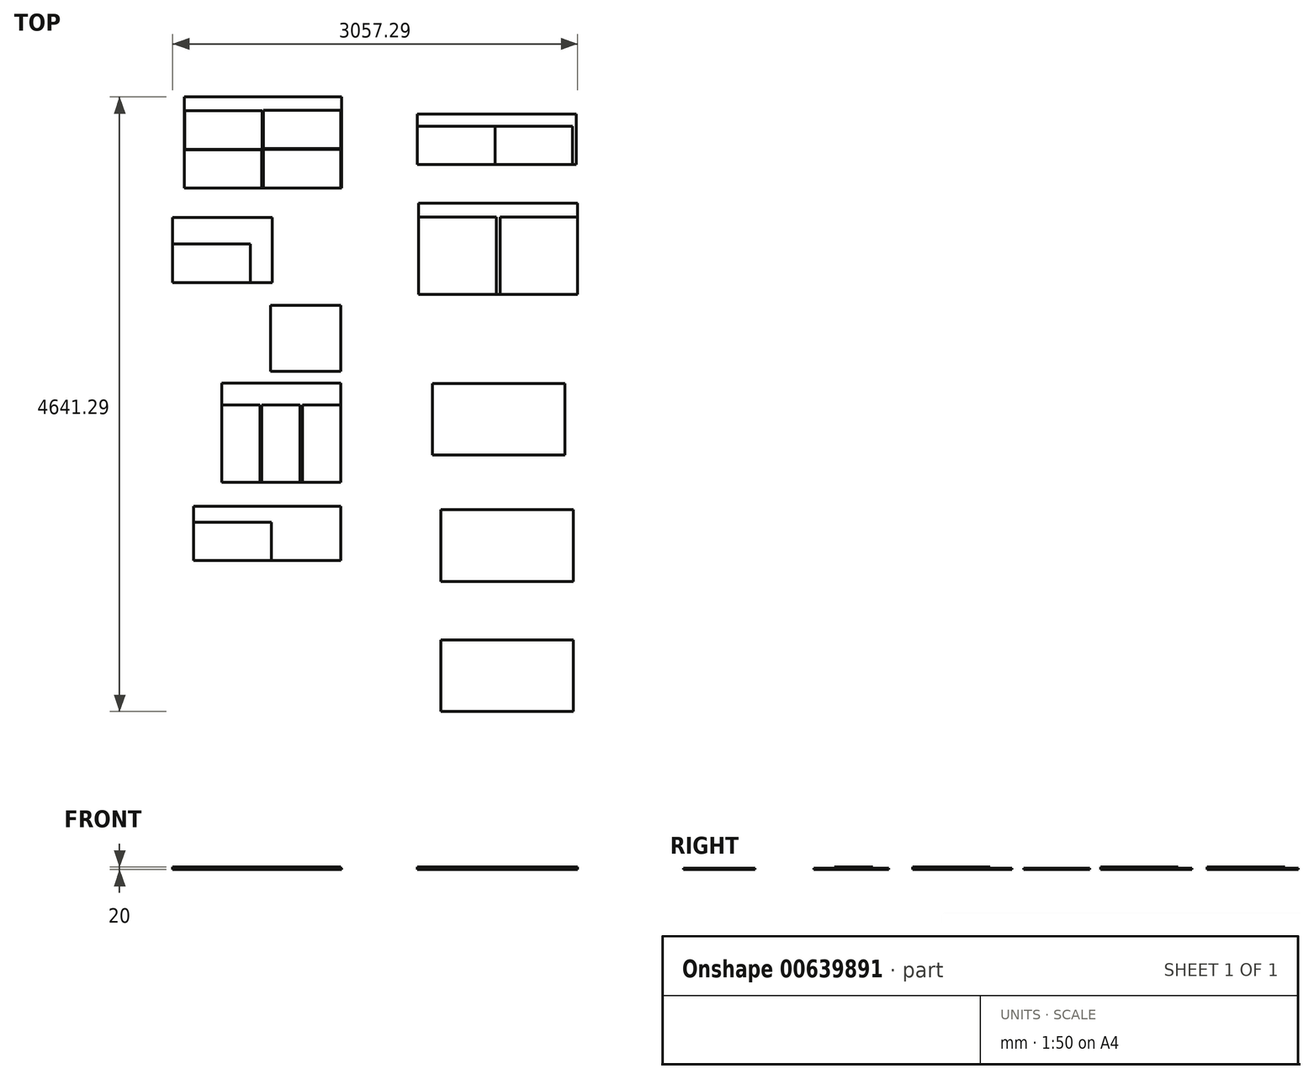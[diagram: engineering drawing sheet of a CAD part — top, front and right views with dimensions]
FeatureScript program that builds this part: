
annotation { "Feature Type Name" : "Feature", "Feature Type Description" : "" }
export const myFeature = defineFeature(function(context is Context, id is Id, definition is map)
    precondition{}
    {
        {
            var Q0;
            Q0=qCreatedBy(makeId("Top.planeOp"),FACE);
            var sketch = newSketch(context, id + "F0", { "sketchPlane" : qUnion([Q0])});
            skLineSegment(sketch, "E0.bottom", {"start": v(-1231.93, 732.64) * mm, "end": v(-41.93, 732.64) * mm});
            skLineSegment(sketch, "E0.top", {"start": v(-1231.93, 42.64) * mm, "end": v(-41.93, 42.64) * mm});
            skLineSegment(sketch, "E0.left", {"start": v(-1231.93, 732.64) * mm, "end": v(-1231.93, 42.64) * mm});
            skLineSegment(sketch, "E0.right", {"start": v(-41.93, 732.64) * mm, "end": v(-41.93, 42.64) * mm});
            skLineSegment(sketch, "E1.bottom", {"start": v(-1318.25, -179.37) * mm, "end": v(-568.25, -179.37) * mm});
            skLineSegment(sketch, "E1.top", {"start": v(-1318.25, -669.37) * mm, "end": v(-568.25, -669.37) * mm});
            skLineSegment(sketch, "E1.left", {"start": v(-1318.25, -179.37) * mm, "end": v(-1318.25, -669.37) * mm});
            skLineSegment(sketch, "E1.right", {"start": v(-568.25, -179.37) * mm, "end": v(-568.25, -669.37) * mm});
            skLineSegment(sketch, "E2.bottom", {"start": v(-579.3, -841.18) * mm, "end": v(-49.3, -841.18) * mm});
            skLineSegment(sketch, "E2.top", {"start": v(-579.3, -1341.18) * mm, "end": v(-49.3, -1341.18) * mm});
            skLineSegment(sketch, "E2.left", {"start": v(-579.3, -841.18) * mm, "end": v(-579.3, -1341.18) * mm});
            skLineSegment(sketch, "E2.right", {"start": v(-49.3, -841.18) * mm, "end": v(-49.3, -1341.18) * mm});
            skLineSegment(sketch, "E3.bottom", {"start": v(-949.3, -1429.12) * mm, "end": v(-49.3, -1429.12) * mm});
            skLineSegment(sketch, "E3.top", {"start": v(-949.3, -2179.12) * mm, "end": v(-49.3, -2179.12) * mm});
            skLineSegment(sketch, "E3.left", {"start": v(-949.3, -1429.12) * mm, "end": v(-949.3, -2179.12) * mm});
            skLineSegment(sketch, "E3.right", {"start": v(-49.3, -1429.12) * mm, "end": v(-49.3, -2179.12) * mm});
            skLineSegment(sketch, "E4.bottom", {"start": v(-1159.3, -2359.48) * mm, "end": v(-49.3, -2359.48) * mm});
            skLineSegment(sketch, "E4.top", {"start": v(-1159.3, -2769.48) * mm, "end": v(-49.3, -2769.48) * mm});
            skLineSegment(sketch, "E4.left", {"start": v(-1159.3, -2359.48) * mm, "end": v(-1159.3, -2769.48) * mm});
            skLineSegment(sketch, "E4.right", {"start": v(-49.3, -2359.48) * mm, "end": v(-49.3, -2769.48) * mm});
            skLineSegment(sketch, "E5.bottom", {"start": v(529.52, 601.78) * mm, "end": v(1729.52, 601.78) * mm});
            skLineSegment(sketch, "E5.top", {"start": v(529.52, 221.78) * mm, "end": v(1729.52, 221.78) * mm});
            skLineSegment(sketch, "E5.left", {"start": v(529.52, 601.78) * mm, "end": v(529.52, 221.78) * mm});
            skLineSegment(sketch, "E5.right", {"start": v(1729.52, 601.78) * mm, "end": v(1729.52, 221.78) * mm});
            skLineSegment(sketch, "E6.bottom", {"start": v(539.04, -70.34) * mm, "end": v(1739.04, -70.34) * mm});
            skLineSegment(sketch, "E6.top", {"start": v(539.04, -760.34) * mm, "end": v(1739.04, -760.34) * mm});
            skLineSegment(sketch, "E6.left", {"start": v(539.04, -70.34) * mm, "end": v(539.04, -760.34) * mm});
            skLineSegment(sketch, "E6.right", {"start": v(1739.04, -70.34) * mm, "end": v(1739.04, -760.34) * mm});
            skLineSegment(sketch, "E7.bottom", {"start": v(641.6, -1432.05) * mm, "end": v(1641.6, -1432.05) * mm});
            skLineSegment(sketch, "E7.top", {"start": v(641.6, -1972.05) * mm, "end": v(1641.6, -1972.05) * mm});
            skLineSegment(sketch, "E7.left", {"start": v(641.6, -1432.05) * mm, "end": v(641.6, -1972.05) * mm});
            skLineSegment(sketch, "E7.right", {"start": v(1641.6, -1432.05) * mm, "end": v(1641.6, -1972.05) * mm});
            skLineSegment(sketch, "E8.bottom", {"start": v(705.36, -2386.14) * mm, "end": v(1705.36, -2386.14) * mm});
            skLineSegment(sketch, "E8.top", {"start": v(705.36, -2926.14) * mm, "end": v(1705.36, -2926.14) * mm});
            skLineSegment(sketch, "E8.left", {"start": v(705.36, -2386.14) * mm, "end": v(705.36, -2926.14) * mm});
            skLineSegment(sketch, "E8.right", {"start": v(1705.36, -2386.14) * mm, "end": v(1705.36, -2926.14) * mm});
            skLineSegment(sketch, "E9.bottom", {"start": v(705.36, -3368.65) * mm, "end": v(1705.36, -3368.65) * mm});
            skLineSegment(sketch, "E9.top", {"start": v(705.36, -3908.65) * mm, "end": v(1705.36, -3908.65) * mm});
            skLineSegment(sketch, "E9.left", {"start": v(705.36, -3368.65) * mm, "end": v(705.36, -3908.65) * mm});
            skLineSegment(sketch, "E9.right", {"start": v(1705.36, -3368.65) * mm, "end": v(1705.36, -3908.65) * mm});
            skLineSegment(sketch, "E10.bottom", {"start": v(5101.56, 951.83) * mm, "end": v(5636.56, 951.83) * mm});
            skLineSegment(sketch, "E10.top", {"start": v(5101.56, 756.83) * mm, "end": v(5636.56, 756.83) * mm});
            skLineSegment(sketch, "E10.left", {"start": v(5101.56, 951.83) * mm, "end": v(5101.56, 756.83) * mm});
            skLineSegment(sketch, "E10.right", {"start": v(5636.56, 951.83) * mm, "end": v(5636.56, 756.83) * mm});
            skLineSegment(sketch, "E11.bottom", {"start": v(5051.56, 290) * mm, "end": v(5636.56, 290) * mm});
            skLineSegment(sketch, "E11.top", {"start": v(5051.56, 0) * mm, "end": v(5636.56, 0) * mm});
            skLineSegment(sketch, "E11.left", {"start": v(5051.56, 290) * mm, "end": v(5051.56, 0) * mm});
            skLineSegment(sketch, "E11.right", {"start": v(5636.56, 290) * mm, "end": v(5636.56, 0) * mm});
            skLineSegment(sketch, "E12.bottom", {"start": v(5684.68, -683.09) * mm, "end": v(6269.68, -683.09) * mm});
            skLineSegment(sketch, "E12.top", {"start": v(5684.68, -1268.09) * mm, "end": v(6269.68, -1268.09) * mm});
            skLineSegment(sketch, "E12.left", {"start": v(5684.68, -683.09) * mm, "end": v(5684.68, -1268.09) * mm});
            skLineSegment(sketch, "E12.right", {"start": v(6269.68, -683.09) * mm, "end": v(6269.68, -1268.09) * mm});
            skLineSegment(sketch, "E13.bottom", {"start": v(4953.65, -683.09) * mm, "end": v(5538.65, -683.09) * mm});
            skLineSegment(sketch, "E13.top", {"start": v(4953.65, -1268.09) * mm, "end": v(5538.65, -1268.09) * mm});
            skLineSegment(sketch, "E13.left", {"start": v(4953.65, -683.09) * mm, "end": v(4953.65, -1268.09) * mm});
            skLineSegment(sketch, "E13.right", {"start": v(5538.65, -683.09) * mm, "end": v(5538.65, -1268.09) * mm});
            skLineSegment(sketch, "E14.bottom", {"start": v(6207.84, 917.61) * mm, "end": v(6742.84, 917.61) * mm});
            skLineSegment(sketch, "E14.top", {"start": v(6207.84, 722.61) * mm, "end": v(6742.84, 722.61) * mm});
            skLineSegment(sketch, "E14.left", {"start": v(6207.84, 917.61) * mm, "end": v(6207.84, 722.61) * mm});
            skLineSegment(sketch, "E14.right", {"start": v(6742.84, 917.61) * mm, "end": v(6742.84, 722.61) * mm});
            skLineSegment(sketch, "E15.bottom", {"start": v(7459.41, 1179.86) * mm, "end": v(7994.41, 1179.86) * mm});
            skLineSegment(sketch, "E15.top", {"start": v(7459.41, 984.86) * mm, "end": v(7994.41, 984.86) * mm});
            skLineSegment(sketch, "E15.left", {"start": v(7459.41, 1179.86) * mm, "end": v(7459.41, 984.86) * mm});
            skLineSegment(sketch, "E15.right", {"start": v(7994.41, 1179.86) * mm, "end": v(7994.41, 984.86) * mm});
            skLineSegment(sketch, "E16.bottom", {"start": v(7949, 782.07) * mm, "end": v(8484, 782.07) * mm});
            skLineSegment(sketch, "E16.top", {"start": v(7949, 587.07) * mm, "end": v(8484, 587.07) * mm});
            skLineSegment(sketch, "E16.left", {"start": v(7949, 782.07) * mm, "end": v(7949, 587.07) * mm});
            skLineSegment(sketch, "E16.right", {"start": v(8484, 782.07) * mm, "end": v(8484, 587.07) * mm});
            skLineSegment(sketch, "E17.bottom", {"start": v(5877.23, 321.61) * mm, "end": v(6462.23, 321.61) * mm});
            skLineSegment(sketch, "E17.top", {"start": v(5877.23, 31.61) * mm, "end": v(6462.23, 31.61) * mm});
            skLineSegment(sketch, "E17.left", {"start": v(5877.23, 321.61) * mm, "end": v(5877.23, 31.61) * mm});
            skLineSegment(sketch, "E17.right", {"start": v(6462.23, 321.61) * mm, "end": v(6462.23, 31.61) * mm});
            skLineSegment(sketch, "E18.bottom", {"start": v(6829.28, 328.04) * mm, "end": v(7414.28, 328.04) * mm});
            skLineSegment(sketch, "E18.top", {"start": v(6829.28, 38.04) * mm, "end": v(7414.28, 38.04) * mm});
            skLineSegment(sketch, "E18.left", {"start": v(6829.28, 328.04) * mm, "end": v(6829.28, 38.04) * mm});
            skLineSegment(sketch, "E18.right", {"start": v(7414.28, 328.04) * mm, "end": v(7414.28, 38.04) * mm});
            skLineSegment(sketch, "E19.bottom", {"start": v(7607.64, 360.2) * mm, "end": v(8192.64, 360.2) * mm});
            skLineSegment(sketch, "E19.top", {"start": v(7607.64, 70.2) * mm, "end": v(8192.64, 70.2) * mm});
            skLineSegment(sketch, "E19.left", {"start": v(7607.64, 360.2) * mm, "end": v(7607.64, 70.2) * mm});
            skLineSegment(sketch, "E19.right", {"start": v(8192.64, 360.2) * mm, "end": v(8192.64, 70.2) * mm});
            skLineSegment(sketch, "E20.bottom", {"start": v(8662.62, 353.77) * mm, "end": v(9247.62, 353.77) * mm});
            skLineSegment(sketch, "E20.top", {"start": v(8662.62, 63.77) * mm, "end": v(9247.62, 63.77) * mm});
            skLineSegment(sketch, "E20.left", {"start": v(8662.62, 353.77) * mm, "end": v(8662.62, 63.77) * mm});
            skLineSegment(sketch, "E20.right", {"start": v(9247.62, 353.77) * mm, "end": v(9247.62, 63.77) * mm});
            skLineSegment(sketch, "E21.bottom", {"start": v(9479.58, 366.64) * mm, "end": v(10064.58, 366.64) * mm});
            skLineSegment(sketch, "E21.top", {"start": v(9479.58, 76.64) * mm, "end": v(10064.58, 76.64) * mm});
            skLineSegment(sketch, "E21.left", {"start": v(9479.58, 366.64) * mm, "end": v(9479.58, 76.64) * mm});
            skLineSegment(sketch, "E21.right", {"start": v(10064.58, 366.64) * mm, "end": v(10064.58, 76.64) * mm});
            skLineSegment(sketch, "E22.bottom", {"start": v(10296.54, 379.5) * mm, "end": v(10881.54, 379.5) * mm});
            skLineSegment(sketch, "E22.top", {"start": v(10296.54, 89.5) * mm, "end": v(10881.54, 89.5) * mm});
            skLineSegment(sketch, "E22.left", {"start": v(10296.54, 379.5) * mm, "end": v(10296.54, 89.5) * mm});
            skLineSegment(sketch, "E22.right", {"start": v(10881.54, 379.5) * mm, "end": v(10881.54, 89.5) * mm});
            skLineSegment(sketch, "E23.bottom", {"start": v(11107.07, 353.77) * mm, "end": v(11692.07, 353.77) * mm});
            skLineSegment(sketch, "E23.top", {"start": v(11107.07, 63.77) * mm, "end": v(11692.07, 63.77) * mm});
            skLineSegment(sketch, "E23.left", {"start": v(11107.07, 353.77) * mm, "end": v(11107.07, 63.77) * mm});
            skLineSegment(sketch, "E23.right", {"start": v(11692.07, 353.77) * mm, "end": v(11692.07, 63.77) * mm});
            skLineSegment(sketch, "E24.bottom", {"start": v(11872.57, 366.64) * mm, "end": v(12457.57, 366.64) * mm});
            skLineSegment(sketch, "E24.top", {"start": v(11872.57, 76.64) * mm, "end": v(12457.57, 76.64) * mm});
            skLineSegment(sketch, "E24.left", {"start": v(11872.57, 366.64) * mm, "end": v(11872.57, 76.64) * mm});
            skLineSegment(sketch, "E24.right", {"start": v(12457.57, 366.64) * mm, "end": v(12457.57, 76.64) * mm});
            skLineSegment(sketch, "E25.bottom", {"start": v(12638.07, 392.37) * mm, "end": v(13223.07, 392.37) * mm});
            skLineSegment(sketch, "E25.top", {"start": v(12638.07, 102.37) * mm, "end": v(13223.07, 102.37) * mm});
            skLineSegment(sketch, "E25.left", {"start": v(12638.07, 392.37) * mm, "end": v(12638.07, 102.37) * mm});
            skLineSegment(sketch, "E25.right", {"start": v(13223.07, 392.37) * mm, "end": v(13223.07, 102.37) * mm});
            skLineSegment(sketch, "E26.bottom", {"start": v(13432.05, 424.54) * mm, "end": v(14017.05, 424.54) * mm});
            skLineSegment(sketch, "E26.top", {"start": v(13432.05, 134.54) * mm, "end": v(14017.05, 134.54) * mm});
            skLineSegment(sketch, "E26.left", {"start": v(13432.05, 424.54) * mm, "end": v(13432.05, 134.54) * mm});
            skLineSegment(sketch, "E26.right", {"start": v(14017.05, 424.54) * mm, "end": v(14017.05, 134.54) * mm});
            skSolve(sketch);
        }
        {
            var Q0;
            Q0=qCreatedBy(makeId("Top.planeOp"),FACE);
            var sketch = newSketch(context, id + "F1", { "sketchPlane" : qUnion([Q0])});
            skLineSegment(sketch, "E27.0.0", {"start": v(-41.93, 732.64) * mm, "end": v(-1231.93, 732.64) * mm});
            skLineSegment(sketch, "E27.0.1", {"start": v(-1231.93, 732.64) * mm, "end": v(-1231.93, 42.64) * mm});
            skLineSegment(sketch, "E27.0.2", {"start": v(-1231.93, 42.64) * mm, "end": v(-41.93, 42.64) * mm});
            skLineSegment(sketch, "E27.0.3", {"start": v(-41.93, 42.64) * mm, "end": v(-41.93, 732.64) * mm});
            skLineSegment(sketch, "E27.1.0", {"start": v(1729.52, 601.78) * mm, "end": v(529.52, 601.78) * mm});
            skLineSegment(sketch, "E27.1.1", {"start": v(529.52, 601.78) * mm, "end": v(529.52, 221.78) * mm});
            skLineSegment(sketch, "E27.1.2", {"start": v(529.52, 221.78) * mm, "end": v(1729.52, 221.78) * mm});
            skLineSegment(sketch, "E27.1.3", {"start": v(1729.52, 221.78) * mm, "end": v(1729.52, 601.78) * mm});
            skLineSegment(sketch, "E27.2.0", {"start": v(1739.04, -70.34) * mm, "end": v(539.04, -70.34) * mm});
            skLineSegment(sketch, "E27.2.1", {"start": v(539.04, -70.34) * mm, "end": v(539.04, -760.34) * mm});
            skLineSegment(sketch, "E27.2.2", {"start": v(539.04, -760.34) * mm, "end": v(1739.04, -760.34) * mm});
            skLineSegment(sketch, "E27.2.3", {"start": v(1739.04, -760.34) * mm, "end": v(1739.04, -70.34) * mm});
            skLineSegment(sketch, "E27.3.0", {"start": v(-568.25, -179.37) * mm, "end": v(-1318.25, -179.37) * mm});
            skLineSegment(sketch, "E27.3.1", {"start": v(-1318.25, -179.37) * mm, "end": v(-1318.25, -669.37) * mm});
            skLineSegment(sketch, "E27.3.2", {"start": v(-1318.25, -669.37) * mm, "end": v(-568.25, -669.37) * mm});
            skLineSegment(sketch, "E27.3.3", {"start": v(-568.25, -669.37) * mm, "end": v(-568.25, -179.37) * mm});
            skLineSegment(sketch, "E27.4.0", {"start": v(-49.3, -841.18) * mm, "end": v(-579.3, -841.18) * mm});
            skLineSegment(sketch, "E27.4.1", {"start": v(-579.3, -841.18) * mm, "end": v(-579.3, -1341.18) * mm});
            skLineSegment(sketch, "E27.4.2", {"start": v(-579.3, -1341.18) * mm, "end": v(-49.3, -1341.18) * mm});
            skLineSegment(sketch, "E27.4.3", {"start": v(-49.3, -1341.18) * mm, "end": v(-49.3, -841.18) * mm});
            skLineSegment(sketch, "E27.5.0", {"start": v(-49.3, -2359.48) * mm, "end": v(-1159.3, -2359.48) * mm});
            skLineSegment(sketch, "E27.5.1", {"start": v(-1159.3, -2359.48) * mm, "end": v(-1159.3, -2769.48) * mm});
            skLineSegment(sketch, "E27.5.2", {"start": v(-1159.3, -2769.48) * mm, "end": v(-49.3, -2769.48) * mm});
            skLineSegment(sketch, "E27.5.3", {"start": v(-49.3, -2769.48) * mm, "end": v(-49.3, -2359.48) * mm});
            skLineSegment(sketch, "E27.6.0", {"start": v(1641.6, -1432.05) * mm, "end": v(641.6, -1432.05) * mm});
            skLineSegment(sketch, "E27.6.1", {"start": v(641.6, -1432.05) * mm, "end": v(641.6, -1972.05) * mm});
            skLineSegment(sketch, "E27.6.2", {"start": v(641.6, -1972.05) * mm, "end": v(1641.6, -1972.05) * mm});
            skLineSegment(sketch, "E27.6.3", {"start": v(1641.6, -1972.05) * mm, "end": v(1641.6, -1432.05) * mm});
            skLineSegment(sketch, "E27.7.0", {"start": v(-49.3, -1429.12) * mm, "end": v(-949.3, -1429.12) * mm});
            skLineSegment(sketch, "E27.7.1", {"start": v(-949.3, -1429.12) * mm, "end": v(-949.3, -2179.12) * mm});
            skLineSegment(sketch, "E27.7.2", {"start": v(-949.3, -2179.12) * mm, "end": v(-49.3, -2179.12) * mm});
            skLineSegment(sketch, "E27.7.3", {"start": v(-49.3, -2179.12) * mm, "end": v(-49.3, -1429.12) * mm});
            skLineSegment(sketch, "E27.8.0", {"start": v(1705.36, -2386.14) * mm, "end": v(705.36, -2386.14) * mm});
            skLineSegment(sketch, "E27.8.1", {"start": v(705.36, -2386.14) * mm, "end": v(705.36, -2926.14) * mm});
            skLineSegment(sketch, "E27.8.2", {"start": v(705.36, -2926.14) * mm, "end": v(1705.36, -2926.14) * mm});
            skLineSegment(sketch, "E27.8.3", {"start": v(1705.36, -2926.14) * mm, "end": v(1705.36, -2386.14) * mm});
            skLineSegment(sketch, "E27.9.0", {"start": v(1705.36, -3368.65) * mm, "end": v(705.36, -3368.65) * mm});
            skLineSegment(sketch, "E27.9.1", {"start": v(705.36, -3368.65) * mm, "end": v(705.36, -3908.65) * mm});
            skLineSegment(sketch, "E27.9.2", {"start": v(705.36, -3908.65) * mm, "end": v(1705.36, -3908.65) * mm});
            skLineSegment(sketch, "E27.9.3", {"start": v(1705.36, -3908.65) * mm, "end": v(1705.36, -3368.65) * mm});
            skLineSegment(sketch, "E28.0.0", {"start": v(1444.5, -1434.15) * mm, "end": v(1444.5, -1969.15) * mm});
            skLineSegment(sketch, "E28.0.1", {"start": v(1444.5, -1969.15) * mm, "end": v(1639.5, -1969.15) * mm});
            skLineSegment(sketch, "E28.0.2", {"start": v(1639.5, -1969.15) * mm, "end": v(1639.5, -1434.15) * mm});
            skLineSegment(sketch, "E28.0.3", {"start": v(1639.5, -1434.15) * mm, "end": v(1444.5, -1434.15) * mm});
            skLineSegment(sketch, "E29.0.0", {"start": v(1240.6, -1434.15) * mm, "end": v(1240.6, -1969.15) * mm});
            skLineSegment(sketch, "E29.0.1", {"start": v(1245.5, -1969.15) * mm, "end": v(1440.5, -1969.15) * mm});
            skLineSegment(sketch, "E29.0.2", {"start": v(1440.5, -1969.15) * mm, "end": v(1440.5, -1434.15) * mm});
            skLineSegment(sketch, "E29.0.3", {"start": v(1440.5, -1434.15) * mm, "end": v(1245.5, -1434.15) * mm});
            skLineSegment(sketch, "E29.1.0", {"start": v(1045.6, -1434.15) * mm, "end": v(1045.6, -1969.15) * mm});
            skLineSegment(sketch, "E29.1.1", {"start": v(1045.6, -1969.15) * mm, "end": v(1240.6, -1969.15) * mm});
            skLineSegment(sketch, "E29.1.2", {"start": v(1245.5, -1969.15) * mm, "end": v(1245.5, -1434.15) * mm});
            skLineSegment(sketch, "E29.1.3", {"start": v(1240.6, -1434.15) * mm, "end": v(1045.6, -1434.15) * mm});
            skLineSegment(sketch, "E29.2.0", {"start": v(843.6, -1434.15) * mm, "end": v(843.6, -1969.15) * mm});
            skLineSegment(sketch, "E29.2.1", {"start": v(843.6, -1969.15) * mm, "end": v(1038.6, -1969.15) * mm});
            skLineSegment(sketch, "E29.2.2", {"start": v(1038.6, -1969.15) * mm, "end": v(1038.6, -1434.15) * mm});
            skLineSegment(sketch, "E29.2.3", {"start": v(1038.6, -1434.15) * mm, "end": v(843.6, -1434.15) * mm});
            skLineSegment(sketch, "E30.0.0", {"start": v(1124.04, -175.34) * mm, "end": v(539.04, -175.34) * mm});
            skLineSegment(sketch, "E30.0.1", {"start": v(539.04, -175.34) * mm, "end": v(539.04, -760.34) * mm});
            skLineSegment(sketch, "E30.0.2", {"start": v(539.04, -760.34) * mm, "end": v(1124.04, -760.34) * mm});
            skLineSegment(sketch, "E30.0.3", {"start": v(1124.04, -760.34) * mm, "end": v(1124.04, -175.34) * mm});
            skLineSegment(sketch, "E30.1.0", {"start": v(1739.04, -175.34) * mm, "end": v(1154.04, -175.34) * mm});
            skLineSegment(sketch, "E30.1.1", {"start": v(1154.04, -175.34) * mm, "end": v(1154.04, -760.34) * mm});
            skLineSegment(sketch, "E30.1.2", {"start": v(1154.04, -760.34) * mm, "end": v(1739.04, -760.34) * mm});
            skLineSegment(sketch, "E30.1.3", {"start": v(1739.04, -760.34) * mm, "end": v(1739.04, -175.34) * mm});
            skLineSegment(sketch, "E31.0.0", {"start": v(-47.93, 631.64) * mm, "end": v(-632.93, 631.64) * mm});
            skLineSegment(sketch, "E31.0.1", {"start": v(-642.93, 627.64) * mm, "end": v(-642.93, 337.64) * mm});
            skLineSegment(sketch, "E31.0.2", {"start": v(-632.93, 335.64) * mm, "end": v(-47.93, 335.64) * mm});
            skLineSegment(sketch, "E31.0.3", {"start": v(-47.93, 341.64) * mm, "end": v(-47.93, 631.64) * mm});
            skLineSegment(sketch, "E31.1.0", {"start": v(-47.93, 341.64) * mm, "end": v(-632.93, 341.64) * mm});
            skLineSegment(sketch, "E31.1.1", {"start": v(-646.93, 332.64) * mm, "end": v(-646.93, 42.64) * mm});
            skLineSegment(sketch, "E31.1.2", {"start": v(-632.93, 45.64) * mm, "end": v(-47.93, 45.64) * mm});
            skLineSegment(sketch, "E31.1.3", {"start": v(-47.93, 45.64) * mm, "end": v(-47.93, 335.64) * mm});
            skLineSegment(sketch, "E31.2.0", {"start": v(-642.93, 627.64) * mm, "end": v(-1227.93, 627.64) * mm});
            skLineSegment(sketch, "E31.2.1", {"start": v(-1227.93, 627.64) * mm, "end": v(-1227.93, 337.64) * mm});
            skLineSegment(sketch, "E31.2.2", {"start": v(-1227.93, 337.64) * mm, "end": v(-642.93, 337.64) * mm});
            skLineSegment(sketch, "E31.2.3", {"start": v(-632.93, 341.64) * mm, "end": v(-632.93, 631.64) * mm});
            skLineSegment(sketch, "E31.3.0", {"start": v(-646.93, 332.64) * mm, "end": v(-1231.93, 332.64) * mm});
            skLineSegment(sketch, "E31.3.1", {"start": v(-1231.93, 332.64) * mm, "end": v(-1231.93, 42.64) * mm});
            skLineSegment(sketch, "E31.3.2", {"start": v(-1231.93, 42.64) * mm, "end": v(-646.93, 42.64) * mm});
            skLineSegment(sketch, "E31.3.3", {"start": v(-632.93, 45.64) * mm, "end": v(-632.93, 335.64) * mm});
            skLineSegment(sketch, "E31.4.0", {"start": v(-339.3, -1594.12) * mm, "end": v(-339.3, -2179.12) * mm});
            skLineSegment(sketch, "E31.4.1", {"start": v(-339.3, -2179.12) * mm, "end": v(-49.3, -2179.12) * mm});
            skLineSegment(sketch, "E31.4.2", {"start": v(-49.3, -2179.12) * mm, "end": v(-49.3, -1594.12) * mm});
            skLineSegment(sketch, "E31.4.3", {"start": v(-49.3, -1594.12) * mm, "end": v(-339.3, -1594.12) * mm});
            skLineSegment(sketch, "E31.5.0", {"start": v(-949.3, -1594.12) * mm, "end": v(-949.3, -2179.12) * mm});
            skLineSegment(sketch, "E31.5.1", {"start": v(-949.3, -2179.12) * mm, "end": v(-659.3, -2179.12) * mm});
            skLineSegment(sketch, "E31.5.2", {"start": v(-659.3, -2179.12) * mm, "end": v(-659.3, -1594.12) * mm});
            skLineSegment(sketch, "E31.5.3", {"start": v(-659.3, -1594.12) * mm, "end": v(-949.3, -1594.12) * mm});
            skLineSegment(sketch, "E31.6.0", {"start": v(-733.25, -379.37) * mm, "end": v(-1318.25, -379.37) * mm});
            skLineSegment(sketch, "E31.6.1", {"start": v(-1318.25, -379.37) * mm, "end": v(-1318.25, -669.37) * mm});
            skLineSegment(sketch, "E31.6.2", {"start": v(-1318.25, -669.37) * mm, "end": v(-733.25, -669.37) * mm});
            skLineSegment(sketch, "E31.6.3", {"start": v(-733.25, -669.37) * mm, "end": v(-733.25, -379.37) * mm});
            skLineSegment(sketch, "E31.7.0", {"start": v(-574.3, -2479.48) * mm, "end": v(-1159.3, -2479.48) * mm});
            skLineSegment(sketch, "E31.7.1", {"start": v(-1159.3, -2479.48) * mm, "end": v(-1159.3, -2769.48) * mm});
            skLineSegment(sketch, "E31.7.2", {"start": v(-1159.3, -2769.48) * mm, "end": v(-574.3, -2769.48) * mm});
            skLineSegment(sketch, "E31.7.3", {"start": v(-574.3, -2769.48) * mm, "end": v(-574.3, -2479.48) * mm});
            skLineSegment(sketch, "E31.8.0", {"start": v(1114.52, 511.78) * mm, "end": v(529.52, 511.78) * mm});
            skLineSegment(sketch, "E31.8.1", {"start": v(529.52, 511.78) * mm, "end": v(529.52, 221.78) * mm});
            skLineSegment(sketch, "E31.8.2", {"start": v(529.52, 221.78) * mm, "end": v(1114.52, 221.78) * mm});
            skLineSegment(sketch, "E31.8.3", {"start": v(1114.52, 221.78) * mm, "end": v(1114.52, 511.78) * mm});
            skLineSegment(sketch, "E31.9.0", {"start": v(1699.52, 511.78) * mm, "end": v(1114.52, 511.78) * mm});
            skLineSegment(sketch, "E31.9.1", {"start": v(1114.52, 511.78) * mm, "end": v(1114.52, 221.78) * mm});
            skLineSegment(sketch, "E31.9.2", {"start": v(1114.52, 221.78) * mm, "end": v(1699.52, 221.78) * mm});
            skLineSegment(sketch, "E31.9.3", {"start": v(1699.52, 221.78) * mm, "end": v(1699.52, 511.78) * mm});
            skLineSegment(sketch, "E31.10.0", {"start": v(-356.93, -2179.12) * mm, "end": v(-356.93, -1594.12) * mm});
            skLineSegment(sketch, "E31.10.1", {"start": v(-356.93, -1594.12) * mm, "end": v(-646.93, -1594.12) * mm});
            skLineSegment(sketch, "E31.10.2", {"start": v(-646.93, -1594.12) * mm, "end": v(-646.93, -2179.12) * mm});
            skLineSegment(sketch, "E31.10.3", {"start": v(-646.93, -2179.12) * mm, "end": v(-356.93, -2179.12) * mm});
            skSolve(sketch);
        }
        {
            var Q0;
            Q0=makeQuery(id+"F0.imprint","IMPRINT",FACE,{"disambiguationData":[TD([[makeQuery(id+"F0.imprint","IMPRINT",EDGE,{"derivedFrom":sQuery(id+"F0.wireOp",EDGE,"E0.bottom")}),-1.0]])]});
            var Q1;
            Q1=makeQuery(id+"F0.imprint","IMPRINT",FACE,{"disambiguationData":[TD([[makeQuery(id+"F0.imprint","IMPRINT",EDGE,{"derivedFrom":sQuery(id+"F0.wireOp",EDGE,"E1.bottom")}),-1.0]])]});
            var Q2;
            Q2=makeQuery(id+"F0.imprint","IMPRINT",FACE,{"disambiguationData":[TD([[makeQuery(id+"F0.imprint","IMPRINT",EDGE,{"derivedFrom":sQuery(id+"F0.wireOp",EDGE,"E2.bottom")}),-1.0]])]});
            var Q3;
            Q3=makeQuery(id+"F0.imprint","IMPRINT",FACE,{"disambiguationData":[TD([[makeQuery(id+"F0.imprint","IMPRINT",EDGE,{"derivedFrom":sQuery(id+"F0.wireOp",EDGE,"E3.bottom")}),-1.0]])]});
            var Q4;
            Q4=makeQuery(id+"F0.imprint","IMPRINT",FACE,{"disambiguationData":[TD([[makeQuery(id+"F0.imprint","IMPRINT",EDGE,{"derivedFrom":sQuery(id+"F0.wireOp",EDGE,"E4.bottom")}),-1.0]])]});
            var Q5;
            Q5=makeQuery(id+"F0.imprint","IMPRINT",FACE,{"disambiguationData":[TD([[makeQuery(id+"F0.imprint","IMPRINT",EDGE,{"derivedFrom":sQuery(id+"F0.wireOp",EDGE,"E5.bottom")}),-1.0]])]});
            var Q6;
            Q6=makeQuery(id+"F0.imprint","IMPRINT",FACE,{"disambiguationData":[TD([[makeQuery(id+"F0.imprint","IMPRINT",EDGE,{"derivedFrom":sQuery(id+"F0.wireOp",EDGE,"E6.bottom")}),-1.0]])]});
            var Q7;
            Q7=makeQuery(id+"F0.imprint","IMPRINT",FACE,{"disambiguationData":[TD([[makeQuery(id+"F0.imprint","IMPRINT",EDGE,{"derivedFrom":sQuery(id+"F0.wireOp",EDGE,"E7.bottom")}),-1.0]])]});
            var Q8;
            Q8=makeQuery(id+"F0.imprint","IMPRINT",FACE,{"disambiguationData":[TD([[makeQuery(id+"F0.imprint","IMPRINT",EDGE,{"derivedFrom":sQuery(id+"F0.wireOp",EDGE,"E8.bottom")}),-1.0]])]});
            var Q9;
            Q9=makeQuery(id+"F0.imprint","IMPRINT",FACE,{"disambiguationData":[TD([[makeQuery(id+"F0.imprint","IMPRINT",EDGE,{"derivedFrom":sQuery(id+"F0.wireOp",EDGE,"E9.bottom")}),-1.0]])]});
            extrude(context, id + "F2", {"entities" : qUnion([Q0, Q1, Q2, Q3, Q4, Q5, Q6, Q7, Q8, Q9]), "oppositeDirection" : true, "depth" : 10 * mm, "offsetDistance" : 25 * mm});
        }
        {
            var Q0;
            Q0=makeQuery(id+"F1.imprint","IMPRINT",FACE,{"disambiguationData":[TD([[makeQuery(id+"F1.imprint","IMPRINT",EDGE,{"derivedFrom":sQuery(id+"F1.wireOp",EDGE,"E31.0.1")}),-1.0]])]});
            var Q1;
            Q1=makeQuery(id+"F1.imprint","IMPRINT",FACE,{"disambiguationData":[TD([[makeQuery(id+"F1.imprint","IMPRINT",EDGE,{"derivedFrom":sQuery(id+"F1.wireOp",EDGE,"E31.0.0")}),1.0]])]});
            var Q2;
            {var subQ5=sQuery(id+"F1.wireOp",EDGE,"E31.1.1");Q2=makeQuery(id+"F1.imprint","IMPRINT",FACE,{"disambiguationData":[TD([[makeQuery(id+"F1.imprint","IMPRINT",EDGE,{"derivedFrom":subQ5}),-1.0]])]});}
            var Q3;
            Q3=makeQuery(id+"F1.imprint","IMPRINT",FACE,{"disambiguationData":[TD([[makeQuery(id+"F1.imprint","IMPRINT",EDGE,{"derivedFrom":sQuery(id+"F1.wireOp",EDGE,"E31.0.2")}),-1.0]])]});
            var Q4;
            {var subQ4=sQuery(id+"F1.wireOp",EDGE,"E31.5.2");Q4=makeQuery(id+"F1.imprint","IMPRINT",FACE,{"disambiguationData":[TD([[makeQuery(id+"F1.imprint","IMPRINT",EDGE,{"derivedFrom":subQ4}),1.0]])]});}
            var Q5;
            {var subQ2=sQuery(id+"F1.wireOp",EDGE,"E31.10.0");Q5=makeQuery(id+"F1.imprint","IMPRINT",FACE,{"disambiguationData":[TD([[makeQuery(id+"F1.imprint","IMPRINT",EDGE,{"derivedFrom":subQ2}),1.0]])]});}
            var Q6;
            {var subQ3=sQuery(id+"F1.wireOp",EDGE,"E31.4.0");Q6=makeQuery(id+"F1.imprint","IMPRINT",FACE,{"disambiguationData":[TD([[makeQuery(id+"F1.imprint","IMPRINT",EDGE,{"derivedFrom":subQ3}),1.0]])]});}
            var Q7;
            {var subQ0=sQuery(id+"F1.wireOp",EDGE,"E31.7.0");Q7=makeQuery(id+"F1.imprint","IMPRINT",FACE,{"disambiguationData":[TD([[makeQuery(id+"F1.imprint","IMPRINT",EDGE,{"derivedFrom":subQ0}),1.0]])]});}
            var Q8;
            {var subQ0=sQuery(id+"F1.wireOp",EDGE,"E31.8.0");Q8=makeQuery(id+"F1.imprint","IMPRINT",FACE,{"disambiguationData":[TD([[makeQuery(id+"F1.imprint","IMPRINT",EDGE,{"derivedFrom":subQ0}),1.0]])]});}
            var Q9;
            Q9=makeQuery(id+"F1.imprint","IMPRINT",FACE,{"disambiguationData":[TD([[makeQuery(id+"F1.imprint","IMPRINT",EDGE,{"derivedFrom":sQuery(id+"F1.wireOp",EDGE,"E31.9.0")}),1.0]])]});
            var Q10;
            {var subQ0=sQuery(id+"F1.wireOp",EDGE,"E30.0.0");Q10=makeQuery(id+"F1.imprint","IMPRINT",FACE,{"disambiguationData":[TD([[makeQuery(id+"F1.imprint","IMPRINT",EDGE,{"derivedFrom":subQ0}),1.0]])]});}
            var Q11;
            {var subQ4=sQuery(id+"F1.wireOp",EDGE,"E30.1.0");Q11=makeQuery(id+"F1.imprint","IMPRINT",FACE,{"disambiguationData":[TD([[makeQuery(id+"F1.imprint","IMPRINT",EDGE,{"derivedFrom":subQ4}),1.0]])]});}
            var Q12;
            {var subQ0=sQuery(id+"F1.wireOp",EDGE,"E29.1.0");Q12=makeQuery(id+"F1.imprint","IMPRINT",FACE,{"disambiguationData":[TD([[makeQuery(id+"F1.imprint","IMPRINT",EDGE,{"derivedFrom":subQ0}),-1.0]])]});}
            var Q13;
            {var subQ0=sQuery(id+"F1.wireOp",EDGE,"E31.6.0");Q13=makeQuery(id+"F1.imprint","IMPRINT",FACE,{"disambiguationData":[TD([[makeQuery(id+"F1.imprint","IMPRINT",EDGE,{"derivedFrom":subQ0}),1.0]])]});}
            var Q14;
            {var subQ0=sQuery(id+"F1.wireOp",EDGE,"E29.0.0");Q14=makeQuery(id+"F1.imprint","IMPRINT",FACE,{"disambiguationData":[TD([[makeQuery(id+"F1.imprint","IMPRINT",EDGE,{"derivedFrom":subQ0}),1.0]])]});}
            extrude(context, id + "F3", {"entities" : qUnion([Q0, Q1, Q2, Q3, Q4, Q5, Q6, Q7, Q8, Q9, Q10, Q11, Q12, Q13, Q14]), "depth" : 10 * mm, "offsetDistance" : 25 * mm});
        }
    });
